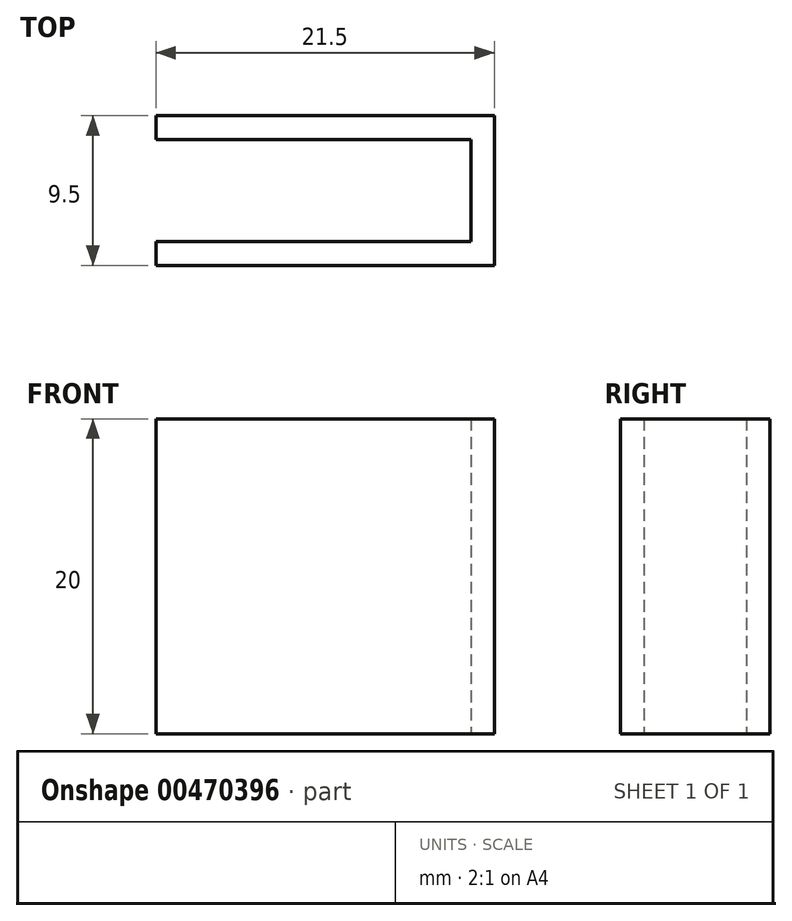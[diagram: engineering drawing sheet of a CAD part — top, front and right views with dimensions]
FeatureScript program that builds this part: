
annotation { "Feature Type Name" : "Feature", "Feature Type Description" : "" }
export const myFeature = defineFeature(function(context is Context, id is Id, definition is map)
    precondition{}
    {
        {
            var Q0;
            Q0=qCreatedBy(makeId("Top.planeOp"),FACE);
            var sketch = newSketch(context, id + "F0", { "sketchPlane" : qUnion([Q0])});
            skPoint(sketch, "E0.middle", {"position": v(0, 0) * mm});
            skLineSegment(sketch, "E1", {"start": v(-10.75, 3.25) * mm, "end": v(-10.75, 4.75) * mm});
            skLineSegment(sketch, "E2", {"start": v(10.75, 4.75) * mm, "end": v(-10.75, 4.75) * mm});
            skLineSegment(sketch, "E3", {"start": v(10.75, -4.75) * mm, "end": v(10.75, 4.75) * mm});
            skLineSegment(sketch, "E4", {"start": v(10.75, -4.75) * mm, "end": v(-10.75, -4.75) * mm});
            skLineSegment(sketch, "E5", {"start": v(-10.75, -4.75) * mm, "end": v(-10.75, -3.25) * mm});
            skLineSegment(sketch, "E6", {"start": v(-10.75, -3.25) * mm, "end": v(9.25, -3.25) * mm});
            skLineSegment(sketch, "E7", {"start": v(9.25, -3.25) * mm, "end": v(9.25, 3.25) * mm});
            skLineSegment(sketch, "E8", {"start": v(-10.75, 3.25) * mm, "end": v(9.25, 3.25) * mm});
            skLineSegment(sketch, "E9", {"start": v(9.25, -3.25) * mm, "end": v(10.75, -3.25) * mm, "construction": true});
            skSolve(sketch);
        }
        {
            var Q0;
            Q0=makeQuery(id+"F0.imprint","IMPRINT",FACE,{"disambiguationData":[TD([[makeQuery(id+"F0.imprint","IMPRINT",EDGE,{"derivedFrom":sQuery(id+"F0.wireOp",EDGE,"E1")}),-1.0]])]});
            extrude(context, id + "F1", {"entities" : qUnion([Q0]), "depth" : 20 * mm, "offsetDistance" : 25 * mm});
        }
    });
